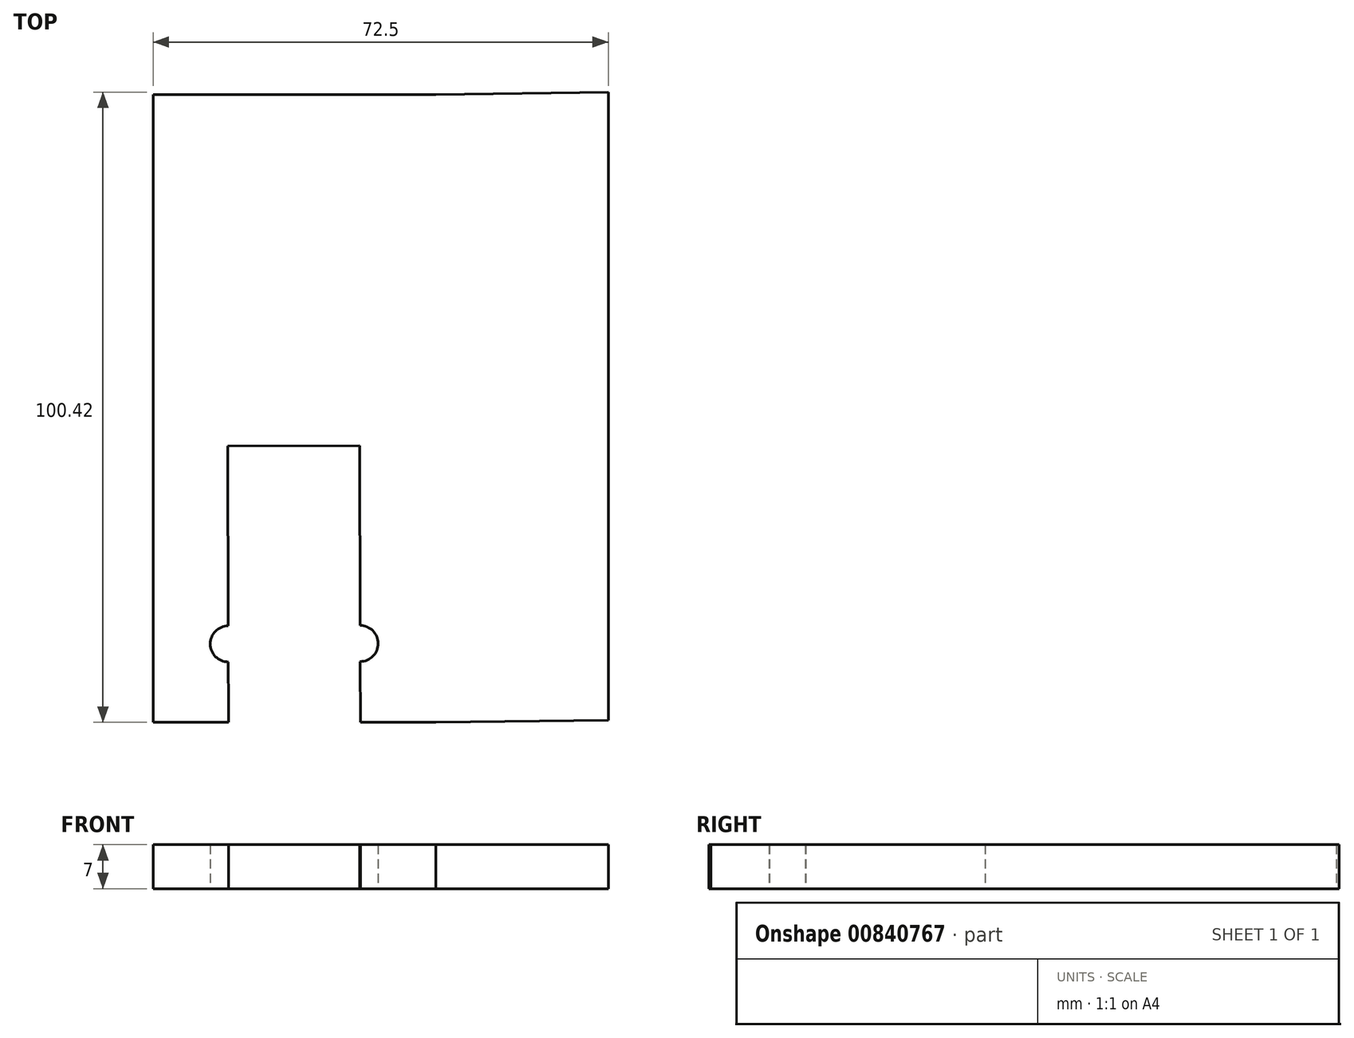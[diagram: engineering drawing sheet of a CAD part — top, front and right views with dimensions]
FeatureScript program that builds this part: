
annotation { "Feature Type Name" : "Feature", "Feature Type Description" : "" }
export const myFeature = defineFeature(function(context is Context, id is Id, definition is map)
    precondition{}
    {
        {
            var Q0;
            Q0=qCreatedBy(makeId("Top.planeOp"),FACE);
            var sketch = newSketch(context, id + "F0", { "sketchPlane" : qUnion([Q0])});
            skLineSegment(sketch, "E0.bottom", {"start": v(22.5, -50) * mm, "end": v(10.5, -50) * mm});
            skLineSegment(sketch, "E0.top", {"start": v(22.5, 50) * mm, "end": v(-22.5, 50) * mm});
            skLineSegment(sketch, "E0.left", {"start": v(22.5, -50) * mm, "end": v(22.5, 50) * mm});
            skLineSegment(sketch, "E0.right", {"start": v(-22.5, -47.25) * mm, "end": v(-22.5, 50) * mm});
            skPoint(sketch, "E0.middle", {"position": v(0, 0) * mm});
            skLineSegment(sketch, "E1.bottom", {"start": v(-10.63, -6) * mm, "end": v(10.37, -5.94) * mm});
            skLineSegment(sketch, "E1.left", {"start": v(-10.63, -6) * mm, "end": v(-10.5, -47.25) * mm});
            skLineSegment(sketch, "E1.right", {"start": v(10.37, -5.94) * mm, "end": v(10.5, -50) * mm});
            skLineSegment(sketch, "E2.top", {"start": v(-22.5, 50) * mm, "end": v(-14.5, 50) * mm});
            skLineSegment(sketch, "E2.left", {"start": v(-22.5, 39) * mm, "end": v(-22.5, 50) * mm});
            skLineSegment(sketch, "E3.left", {"start": v(-22.5, 16) * mm, "end": v(-22.5, 10) * mm});
            skPoint(sketch, "E4", {"position": v(-17.77, -42) * mm});
            skPoint(sketch, "E5", {"position": v(-17.07, -10) * mm});
            skPoint(sketch, "E6", {"position": v(17.93, -12) * mm});
            skPoint(sketch, "E7", {"position": v(17.73, -44) * mm});
            skPoint(sketch, "E8.positionSnap0", {"position": v(-18.5, 50) * mm});
            skPoint(sketch, "E9", {"position": v(-10.54, -37.5) * mm});
            skPoint(sketch, "E10", {"position": v(0, 50) * mm});
            skPoint(sketch, "E11", {"position": v(22.5, 17.15) * mm});
            skPoint(sketch, "E12", {"position": v(10.46, -37.44) * mm});
            skLineSegment(sketch, "E13", {"start": v(0, -64.42) * mm, "end": v(0, 71.46) * mm, "construction": true});
            skPoint(sketch, "E14", {"position": v(-22.5, -44) * mm});
            skPoint(sketch, "E15", {"position": v(-22.5, -47.25) * mm});
            skLineSegment(sketch, "E16", {"start": v(-22.5, -47.25) * mm, "end": v(-10.5, -47.25) * mm});
            skPoint(sketch, "E17.trimOffspring.end.orphan", {"position": v(-22.5, -50) * mm});
            skLineSegment(sketch, "E18.MirrorCS", {"start": v(-22.5, -50) * mm, "end": v(-10.5, -50) * mm});
            skLineSegment(sketch, "E19", {"start": v(-22.5, -50) * mm, "end": v(-22.5, -47.25) * mm});
            skLineSegment(sketch, "E20", {"start": v(-10.5, -50) * mm, "end": v(-10.5, -47.25) * mm});
            skLineSegment(sketch, "E21", {"start": v(50, 50.42) * mm, "end": v(50, -49.64) * mm});
            skLineSegment(sketch, "E22", {"start": v(22.5, 50) * mm, "end": v(50, 50.42) * mm});
            skLineSegment(sketch, "E23", {"start": v(50, -49.64) * mm, "end": v(22.5, -50) * mm});
            skLineSegment(sketch, "E24.MirrorCS", {"start": v(-22.5, 50) * mm, "end": v(-50, 50.42) * mm});
            skLineSegment(sketch, "E25.MirrorCS", {"start": v(-50, 50.42) * mm, "end": v(-50, -49.64) * mm});
            skLineSegment(sketch, "E26.MirrorCS", {"start": v(-50, -49.64) * mm, "end": v(-22.5, -50) * mm});
            skSolve(sketch);
        }
        {
            var Q0;
            Q0=makeQuery(id+"F0.imprint","IMPRINT",FACE,{"disambiguationData":[TD([[makeQuery(id+"F0.imprint","IMPRINT",EDGE,{"derivedFrom":sQuery(id+"F0.wireOp",EDGE,"E0.bottom")}),-1.0]])]});
            var Q1;
            Q1=makeQuery(id+"F0.imprint","IMPRINT",FACE,{"disambiguationData":[TD([[makeQuery(id+"F0.imprint","IMPRINT",EDGE,{"derivedFrom":sQuery(id+"F0.wireOp",EDGE,"E16")}),-1.0]])]});
            var Q2;
            {var subQ1=sQuery(id+"F0.wireOp",EDGE,"E2.left");Q2=makeQuery(id+"F0.imprint","IMPRINT",FACE,{"disambiguationData":[TD([[makeQuery(id+"F0.imprint","IMPRINT",EDGE,{"derivedFrom":subQ1}),1.0]])]});}
            var Q3;
            Q3=makeQuery(id+"F0.imprint","IMPRINT",FACE,{"disambiguationData":[TD([[makeQuery(id+"F0.imprint","IMPRINT",EDGE,{"derivedFrom":sQuery(id+"F0.wireOp",EDGE,"E0.left")}),-1.0]])]});
            extrude(context, id + "F1", {"entities" : qUnion([Q0, Q1, Q2, Q3]), "offsetDistance" : 25 * mm, "depth" : 7 * mm});
        }
        {
            var Q0;
            Q0=sQuery(id+"F0.wireOp",VERTEX,"E9");
            var Q1;
            Q1=sQuery(id+"F0.wireOp",VERTEX,"E12");
            var Q2;
            Q2=makeQuery(id+"F1.opExtrude","SWEPT_BODY",BODY,{"disambiguationData":[OSD([sQuery(id+"F0.wireOp",EDGE,"E0.bottom"),sQuery(id+"F0.wireOp",EDGE,"E0.top"),sQuery(id+"F0.wireOp",EDGE,"E0.left"),sQuery(id+"F0.wireOp",EDGE,"E0.right"),sQuery(id+"F0.wireOp",EDGE,"E1.bottom"),sQuery(id+"F0.wireOp",EDGE,"E1.left"),sQuery(id+"F0.wireOp",EDGE,"E1.right"),sQuery(id+"F0.wireOp",EDGE,"E2.bottom"),sQuery(id+"F0.wireOp",EDGE,"E2.right"),sQuery(id+"F0.wireOp",EDGE,"E3.bottom"),sQuery(id+"F0.wireOp",EDGE,"E3.top"),sQuery(id+"F0.wireOp",EDGE,"E3.right"),sQuery(id+"F0.wireOp",EDGE,"E17.trimOffspring")])]});
            hole(context, id + "F2", {"style" : HoleStyle.SIMPLE, "endStyle" : HoleEndStyle.THROUGH, "oppositeDirection" : true, "holeDiameter" : 5.75 * mm, "isTappedThrough" : true, "tappedDepth" : 12.7 * mm, "tapClearance" : 3, "locations" : qUnion([Q0, Q1]), "scope" : qUnion([Q2])});
        }
    });
